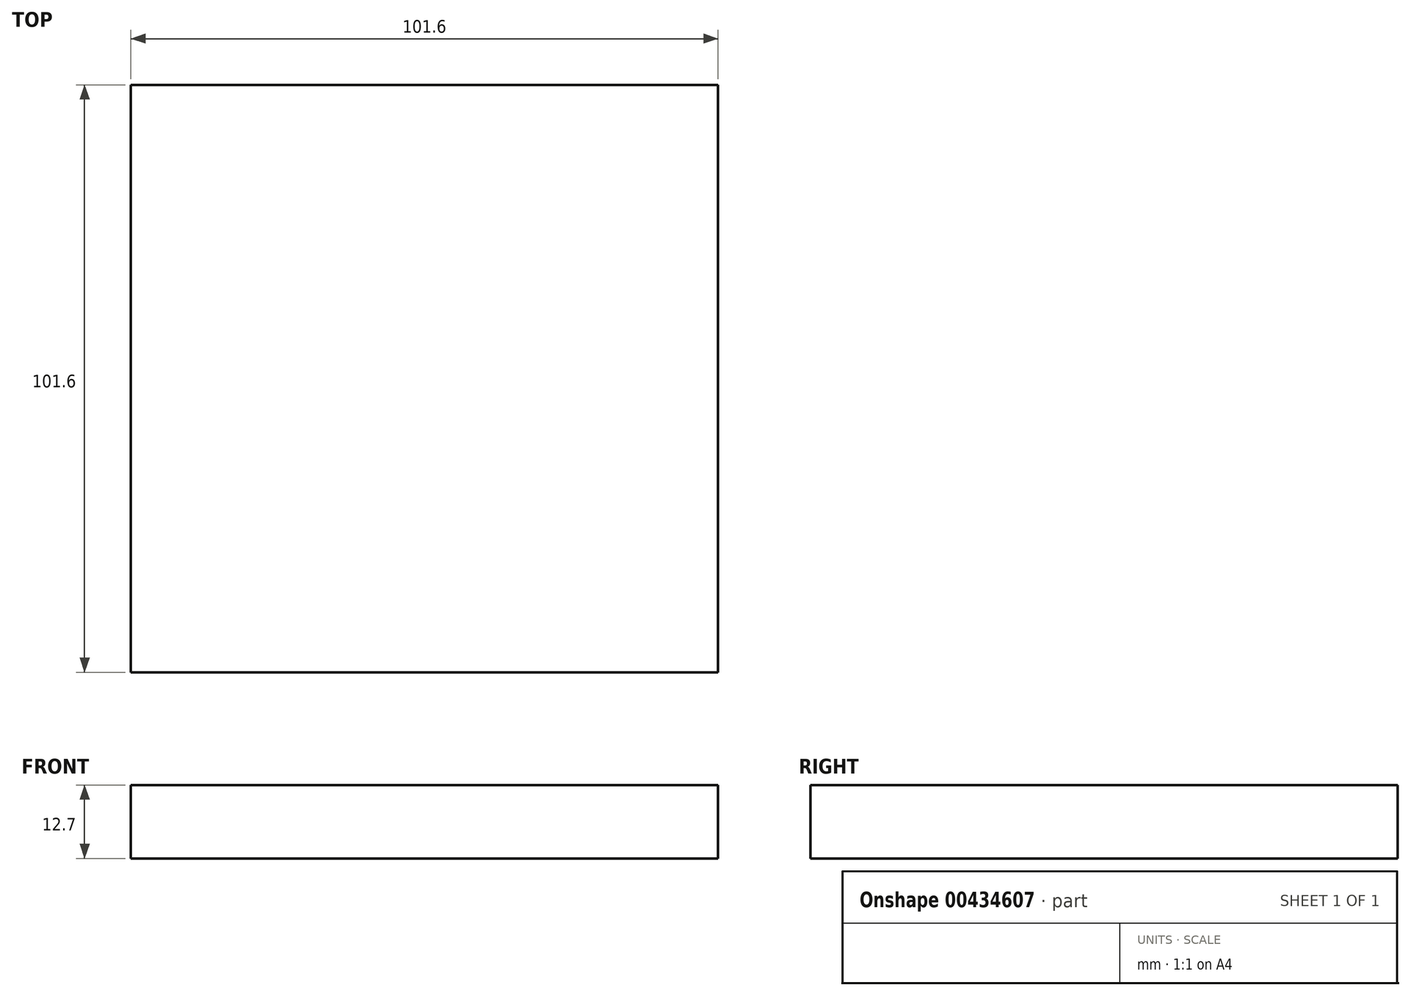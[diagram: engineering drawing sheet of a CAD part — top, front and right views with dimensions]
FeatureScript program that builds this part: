
annotation { "Feature Type Name" : "Feature", "Feature Type Description" : "" }
export const myFeature = defineFeature(function(context is Context, id is Id, definition is map)
    precondition{}
    {
        {
            var Q0;
            Q0=qCreatedBy(makeId("Top.planeOp"),FACE);
            var sketch = newSketch(context, id + "F0", { "sketchPlane" : qUnion([Q0])});
            skLineSegment(sketch, "E0.bottom", {"start": v(50.8, 50.8) * mm, "end": v(-50.8, 50.8) * mm});
            skLineSegment(sketch, "E0.top", {"start": v(50.8, -50.8) * mm, "end": v(-50.8, -50.8) * mm});
            skLineSegment(sketch, "E0.left", {"start": v(50.8, 50.8) * mm, "end": v(50.8, -50.8) * mm});
            skLineSegment(sketch, "E0.right", {"start": v(-50.8, 50.8) * mm, "end": v(-50.8, -50.8) * mm});
            skPoint(sketch, "E0.middle", {"position": v(0, 0) * mm});
            skSolve(sketch);
        }
        {
            var Q0;
            Q0=makeQuery(id+"F0.imprint","IMPRINT",FACE,{"disambiguationData":[TD([[makeQuery(id+"F0.imprint","IMPRINT",EDGE,{"derivedFrom":sQuery(id+"F0.wireOp",EDGE,"E0.bottom")}),1.0]])]});
            extrude(context, id + "F1", {"entities" : qUnion([Q0]), "depth" : 12.7 * mm});
        }
    });
